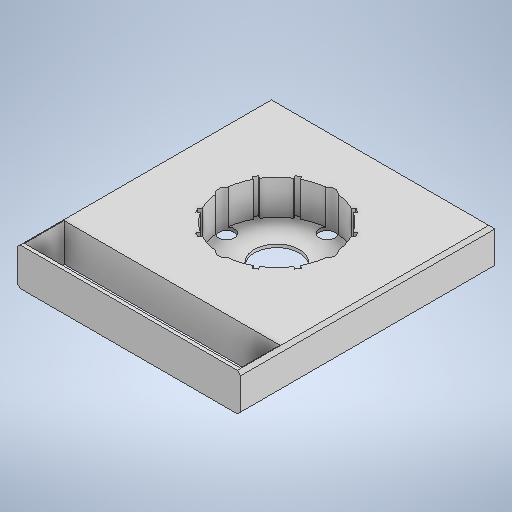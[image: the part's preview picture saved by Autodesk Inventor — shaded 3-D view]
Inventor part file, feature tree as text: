
AUTODESK INVENTOR PART (.ipt)
format: ipt  version: 2025.1 (Build 291241000, 241)  size: 337,920 bytes
history: native  units: mm
features: sketch x6, extrude x4, chamfer x1
ambient origin geometry x8: Origin, YZ Plane, XZ Plane, XY Plane, X Axis, Y Axis, Z Axis, Center Point
bodies: Volumenkörper1 (feature_tree)
feature tree (11):
  extrude  "Extrusion1"  Depth=21.9mm TaperAngle=45.0deg
  chamfer  "Fasen1"  Distance=21.9mm
  extrude  "Extrusion2"  Depth=10.0mm TaperAngle=360.0deg
  extrude  "Extrusion3"  Depth=3.0mm TaperAngle=360.0deg
  extrude  "Extrusion4"  Depth=25.0mm
  sketch  "Skizze1"  dims[d0=23.85mm d1=0.0mm d2=2.0mm d3=2.0mm d4=45.0deg d5=70.05mm d6=21.9mm d7=0.0mm]
  sketch  "Skizze2"  dims[d15=120.0mm d16=3.0mm d17=74.0mm d18=360.0deg]
  sketch  "Skizze3"  dims[d22=160.8mm]
  sketch  "Skizze - Runde Anordnung1"  dims[d9=40.0mm d10=10.0mm d11=360.0deg d12=12.9mm d13=0.0mm]
  sketch  "Skizze4"  dims[d23=141.3mm d24=28.5mm d25=2.2mm]
  sketch  "Skizze - Runde Anordnung2"  dims[d19=10.0mm d20=0.0mm d21=25.0mm]
